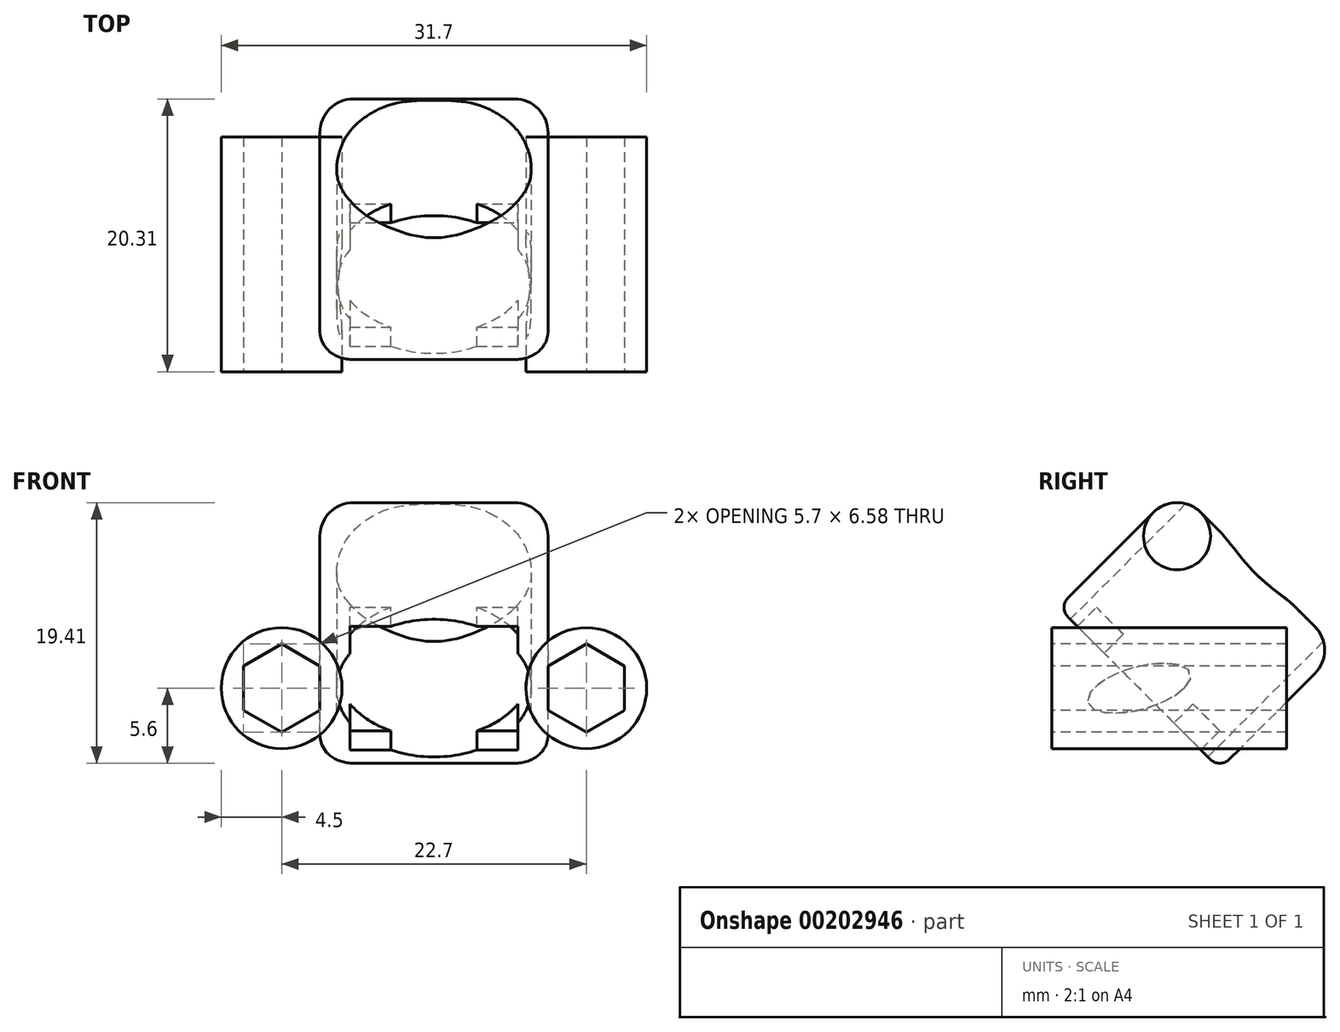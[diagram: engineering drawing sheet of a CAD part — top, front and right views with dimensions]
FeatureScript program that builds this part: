
annotation { "Feature Type Name" : "Feature", "Feature Type Description" : "" }
export const myFeature = defineFeature(function(context is Context, id is Id, definition is map)
    precondition{}
    {
        {
            var Q0;
            Q0=qCreatedBy(makeId("Top.planeOp"),FACE);
            var sketch = newSketch(context, id + "F0", { "sketchPlane" : qUnion([Q0])});
            skLineSegment(sketch, "E0.bottom", {"start": v(6.25, 6.25) * mm, "end": v(-6.25, 6.25) * mm});
            skLineSegment(sketch, "E0.top", {"start": v(6.25, -6.25) * mm, "end": v(-6.25, -6.25) * mm});
            skLineSegment(sketch, "E0.left", {"start": v(6.25, 6.25) * mm, "end": v(6.25, -6.25) * mm});
            skLineSegment(sketch, "E0.right", {"start": v(-6.25, 6.25) * mm, "end": v(-6.25, -6.25) * mm});
            skPoint(sketch, "E0.middle", {"position": v(0, 0) * mm});
            skCircle(sketch, "E1", {"center": v(0, 0) * mm, "radius": 7.25 * mm});
            skLineSegment(sketch, "E2.bottom", {"start": v(8.5, 8.5) * mm, "end": v(-8.5, 8.5) * mm});
            skLineSegment(sketch, "E2.top", {"start": v(8.5, -8.5) * mm, "end": v(-8.5, -8.5) * mm});
            skLineSegment(sketch, "E2.left", {"start": v(8.5, 8.5) * mm, "end": v(8.5, -8.5) * mm});
            skLineSegment(sketch, "E2.right", {"start": v(-8.5, 8.5) * mm, "end": v(-8.5, -8.5) * mm});
            skSolve(sketch);
        }
        {
            var Q0;
            Q0=makeQuery(id+"F0.imprint","IMPRINT",FACE,{"disambiguationData":[TD([[makeQuery(id+"F0.imprint","IMPRINT",EDGE,{"derivedFrom":sQuery(id+"F0.wireOp",EDGE,"E2.bottom")}),1.0]])]});
            var Q1;
            {var subQ0=sQuery(id+"F0.wireOp",EDGE,"E0.right");var subQ1=sQuery(id+"F0.wireOp",EDGE,"E0.bottom");var subQ2=makeQuery(id+"F0.imprint","INTERSECT",VERTEX,{"derivedFrom":[subQ1,subQ0]});Q1=makeQuery(id+"F0.imprint","IMPRINT",FACE,{"disambiguationData":[TD([[makeQuery(id+"F0.imprint","IMPRINT",EDGE,{"disambiguationData":[TD([[subQ2,1.0]])],"derivedFrom":subQ1}),1.0]])]});}
            var Q2;
            {var subQ0=sQuery(id+"F0.wireOp",EDGE,"E0.left");var subQ1=sQuery(id+"F0.wireOp",EDGE,"E0.bottom");var subQ2=makeQuery(id+"F0.imprint","INTERSECT",VERTEX,{"derivedFrom":[subQ1,subQ0]});Q2=makeQuery(id+"F0.imprint","IMPRINT",FACE,{"disambiguationData":[TD([[makeQuery(id+"F0.imprint","IMPRINT",EDGE,{"disambiguationData":[TD([[subQ2,-1.0]])],"derivedFrom":subQ1}),1.0]])]});}
            var Q3;
            {var subQ0=sQuery(id+"F0.wireOp",EDGE,"E0.left");var subQ1=sQuery(id+"F0.wireOp",EDGE,"E0.top");var subQ2=makeQuery(id+"F0.imprint","INTERSECT",VERTEX,{"derivedFrom":[subQ1,subQ0]});Q3=makeQuery(id+"F0.imprint","IMPRINT",FACE,{"disambiguationData":[TD([[makeQuery(id+"F0.imprint","IMPRINT",EDGE,{"disambiguationData":[TD([[subQ2,-1.0]])],"derivedFrom":subQ1}),-1.0]])]});}
            var Q4;
            {var subQ0=sQuery(id+"F0.wireOp",EDGE,"E0.right");var subQ1=sQuery(id+"F0.wireOp",EDGE,"E0.top");var subQ2=makeQuery(id+"F0.imprint","INTERSECT",VERTEX,{"derivedFrom":[subQ1,subQ0]});Q4=makeQuery(id+"F0.imprint","IMPRINT",FACE,{"disambiguationData":[TD([[makeQuery(id+"F0.imprint","IMPRINT",EDGE,{"disambiguationData":[TD([[subQ2,1.0]])],"derivedFrom":subQ1}),-1.0]])]});}
            extrude(context, id + "F1", {"entities" : qUnion([Q0, Q1, Q2, Q3, Q4]), "depth" : 12.5 * mm});
        }
        {
            var Q0;
            Q0=qCreatedBy(makeId("Top.planeOp"),FACE);
            var sketch = newSketch(context, id + "F2", { "sketchPlane" : qUnion([Q0])});
            skLineSegment(sketch, "E3", {"start": v(-15.14, 0) * mm, "end": v(14.33, 0) * mm});
            skSolve(sketch);
        }
        {
            var Q0;
            Q0=qCreatedBy(makeId("Front.planeOp"),FACE);
            var sketch = newSketch(context, id + "F3", { "sketchPlane" : qUnion([Q0])});
            skCircle(sketch, "E4", {"center": v(-11.35, 0) * mm, "radius": 4.5 * mm});
            skCircle(sketch, "E5.cCircle", {"center": v(-11.35, 0) * mm, "radius": 2.85 * mm, "construction": true});
            skLineSegment(sketch, "E5.0", {"start": v(-8.5, 1.65) * mm, "end": v(-8.5, -1.65) * mm});
            skLineSegment(sketch, "E5.1", {"start": v(-8.5, -1.65) * mm, "end": v(-11.35, -3.3) * mm});
            skLineSegment(sketch, "E5.2", {"start": v(-11.35, -3.3) * mm, "end": v(-14.2, -1.65) * mm});
            skLineSegment(sketch, "E5.3", {"start": v(-14.2, -1.65) * mm, "end": v(-14.2, 1.65) * mm});
            skLineSegment(sketch, "E5.4", {"start": v(-14.2, 1.65) * mm, "end": v(-11.35, 3.3) * mm});
            skLineSegment(sketch, "E5.5", {"start": v(-11.35, 3.3) * mm, "end": v(-8.5, 1.65) * mm});
            skPoint(sketch, "E5.0.midPoint", {"position": v(-8.5, 0) * mm});
            skCircle(sketch, "E6.1.0.0", {"center": v(11.35, 0) * mm, "radius": 4.5 * mm});
            skLineSegment(sketch, "E6.direction1", {"start": v(-11.35, 0) * mm, "end": v(11.35, 0) * mm, "construction": true});
            skLineSegment(sketch, "E7.1.0.0", {"start": v(11.35, -3.3) * mm, "end": v(8.5, -1.65) * mm});
            skLineSegment(sketch, "E7.1.0.1", {"start": v(14.2, -1.65) * mm, "end": v(11.35, -3.3) * mm});
            skLineSegment(sketch, "E7.1.0.2", {"start": v(14.2, 1.65) * mm, "end": v(14.2, -1.65) * mm});
            skLineSegment(sketch, "E7.1.0.3", {"start": v(11.35, 3.3) * mm, "end": v(14.2, 1.65) * mm});
            skLineSegment(sketch, "E7.1.0.4", {"start": v(8.5, 1.65) * mm, "end": v(11.35, 3.3) * mm});
            skLineSegment(sketch, "E7.1.0.5", {"start": v(8.5, -1.65) * mm, "end": v(8.5, 1.65) * mm});
            skLineSegment(sketch, "E7.direction1", {"start": v(-14.2, -1.65) * mm, "end": v(8.5, -1.65) * mm, "construction": true});
            skPoint(sketch, "E8.0.1.0", {"position": v(-8.5, -41.3) * mm});
            skLineSegment(sketch, "E8.0.1.2", {"start": v(11.35, -38) * mm, "end": v(14.2, -39.65) * mm});
            skLineSegment(sketch, "E8.0.1.3", {"start": v(8.5, -39.65) * mm, "end": v(11.35, -38) * mm});
            skLineSegment(sketch, "E8.0.1.4", {"start": v(8.5, -42.95) * mm, "end": v(8.5, -39.65) * mm});
            skCircle(sketch, "E8.0.1.5", {"center": v(-11.35, -41.3) * mm, "radius": 4.5 * mm});
            skCircle(sketch, "E8.0.1.6", {"center": v(-11.35, -41.3) * mm, "radius": 2.85 * mm, "construction": true});
            skCircle(sketch, "E8.0.1.7", {"center": v(11.35, -41.3) * mm, "radius": 4.5 * mm});
            skLineSegment(sketch, "E8.0.1.8", {"start": v(-11.35, -41.3) * mm, "end": v(11.35, -41.3) * mm, "construction": true});
            skLineSegment(sketch, "E8.0.1.9", {"start": v(11.35, -44.6) * mm, "end": v(8.5, -42.95) * mm});
            skLineSegment(sketch, "E8.0.1.10", {"start": v(14.2, -42.95) * mm, "end": v(11.35, -44.6) * mm});
            skLineSegment(sketch, "E8.0.1.11", {"start": v(14.2, -39.65) * mm, "end": v(14.2, -42.95) * mm});
            skLineSegment(sketch, "E8.0.1.12", {"start": v(-8.5, -39.65) * mm, "end": v(-8.5, -42.95) * mm});
            skLineSegment(sketch, "E8.0.1.13", {"start": v(-8.5, -42.95) * mm, "end": v(-11.35, -44.6) * mm});
            skLineSegment(sketch, "E8.0.1.14", {"start": v(-11.35, -44.6) * mm, "end": v(-14.2, -42.95) * mm});
            skLineSegment(sketch, "E8.0.1.15", {"start": v(-14.2, -42.95) * mm, "end": v(-14.2, -39.65) * mm});
            skLineSegment(sketch, "E8.0.1.16", {"start": v(-14.2, -39.65) * mm, "end": v(-11.35, -38) * mm});
            skLineSegment(sketch, "E8.0.1.17", {"start": v(-11.35, -38) * mm, "end": v(-8.5, -39.65) * mm});
            skLineSegment(sketch, "E8.direction1", {"start": v(-14.2, -1.65) * mm, "end": v(10.8, -1.65) * mm, "construction": true});
            skLineSegment(sketch, "E8.direction2", {"start": v(-14.2, -1.65) * mm, "end": v(-14.2, -42.95) * mm, "construction": true});
            skLineSegment(sketch, "E9", {"start": v(22.71, -41.3) * mm, "end": v(-23, -41.3) * mm, "construction": true});
            skArc(sketch, "E10", {"start": v(15.85, -41.3) * mm, "mid": v(16.07, -41.21) * mm, "end": v(16.28, -41.13) * mm});
            skLineSegment(sketch, "E11.bottom", {"start": v(-18, -2.65) * mm, "end": v(18, -2.65) * mm});
            skLineSegment(sketch, "E11.top", {"start": v(-18, -38.65) * mm, "end": v(18, -38.65) * mm});
            skLineSegment(sketch, "E11.left", {"start": v(-18, -2.65) * mm, "end": v(-18, -38.65) * mm});
            skLineSegment(sketch, "E11.right", {"start": v(18, -2.65) * mm, "end": v(18, -38.65) * mm});
            skPoint(sketch, "E11.middle", {"position": v(0, -20.65) * mm});
            skLineSegment(sketch, "E12", {"start": v(20, -5.72) * mm, "end": v(20, -35.58) * mm});
            skArc(sketch, "E13.trimOffspring", {"start": v(16.28, -0.17) * mm, "mid": v(16.07, -0.09) * mm, "end": v(15.85, 0) * mm});
            skPoint(sketch, "E14.visualSharp", {"position": v(20, -2.13) * mm});
            skArc(sketch, "E14.filletArc", {"start": v(20, -5.72) * mm, "mid": v(18.98, -2.38) * mm, "end": v(16.28, -0.17) * mm});
            skPoint(sketch, "E15.visualSharp", {"position": v(20, -39.17) * mm});
            skArc(sketch, "E15.filletArc", {"start": v(16.28, -41.13) * mm, "mid": v(18.98, -38.92) * mm, "end": v(20, -35.58) * mm});
            skArc(sketch, "E16.0", {"start": v(15.55, -42.92) * mm, "mid": v(19.83, -40.3) * mm, "end": v(21.5, -35.58) * mm});
            skLineSegment(sketch, "E16.1", {"start": v(21.5, -5.72) * mm, "end": v(21.5, -35.58) * mm});
            skArc(sketch, "E16.2", {"start": v(21.5, -5.72) * mm, "mid": v(19.83, -1) * mm, "end": v(15.55, 1.62) * mm});
            skArc(sketch, "E17.MirrorCS", {"start": v(-16.28, -0.17) * mm, "mid": v(-16.07, -0.09) * mm, "end": v(-15.85, 0) * mm});
            skArc(sketch, "E18.MirrorCS", {"start": v(-15.85, -41.3) * mm, "mid": v(-16.07, -41.21) * mm, "end": v(-16.28, -41.13) * mm});
            skArc(sketch, "E19.MirrorCS", {"start": v(-16.28, -41.13) * mm, "mid": v(-18.98, -38.92) * mm, "end": v(-20, -35.58) * mm});
            skArc(sketch, "E20.MirrorCS", {"start": v(-15.55, -42.92) * mm, "mid": v(-19.83, -40.3) * mm, "end": v(-21.5, -35.58) * mm});
            skArc(sketch, "E21.MirrorCS", {"start": v(-21.5, -5.72) * mm, "mid": v(-19.83, -1) * mm, "end": v(-15.55, 1.62) * mm});
            skArc(sketch, "E22.MirrorCS", {"start": v(-20, -5.72) * mm, "mid": v(-18.98, -2.38) * mm, "end": v(-16.28, -0.17) * mm});
            skLineSegment(sketch, "E23.MirrorCS", {"start": v(-21.5, -5.72) * mm, "end": v(-21.5, -35.58) * mm});
            skLineSegment(sketch, "E24.MirrorCS", {"start": v(-20, -5.72) * mm, "end": v(-20, -35.58) * mm});
            skLineSegment(sketch, "E25", {"start": v(7.16, -42.95) * mm, "end": v(-7.16, -42.95) * mm});
            skLineSegment(sketch, "E26.0", {"start": v(6.85, -41.45) * mm, "end": v(-6.85, -41.45) * mm});
            skSolve(sketch);
        }
        {
            var Q0;
            {var subQ0=sQuery(id+"F0.wireOp",EDGE,"E0.left");var subQ1=sQuery(id+"F0.wireOp",EDGE,"E0.bottom");var subQ2=makeQuery(id+"F0.imprint","INTERSECT",VERTEX,{"derivedFrom":[subQ1,subQ0]});Q0=makeQuery(id+"F0.imprint","IMPRINT",FACE,{"disambiguationData":[TD([[makeQuery(id+"F0.imprint","IMPRINT",EDGE,{"disambiguationData":[TD([[subQ2,-1.0]])],"derivedFrom":subQ1}),1.0]])]});}
            var Q1;
            {var subQ0=sQuery(id+"F0.wireOp",EDGE,"E0.right");var subQ1=sQuery(id+"F0.wireOp",EDGE,"E0.bottom");var subQ2=makeQuery(id+"F0.imprint","INTERSECT",VERTEX,{"derivedFrom":[subQ1,subQ0]});Q1=makeQuery(id+"F0.imprint","IMPRINT",FACE,{"disambiguationData":[TD([[makeQuery(id+"F0.imprint","IMPRINT",EDGE,{"disambiguationData":[TD([[subQ2,1.0]])],"derivedFrom":subQ1}),1.0]])]});}
            var Q2;
            {var subQ0=sQuery(id+"F0.wireOp",EDGE,"E0.right");var subQ1=sQuery(id+"F0.wireOp",EDGE,"E0.top");var subQ2=makeQuery(id+"F0.imprint","INTERSECT",VERTEX,{"derivedFrom":[subQ1,subQ0]});Q2=makeQuery(id+"F0.imprint","IMPRINT",FACE,{"disambiguationData":[TD([[makeQuery(id+"F0.imprint","IMPRINT",EDGE,{"disambiguationData":[TD([[subQ2,1.0]])],"derivedFrom":subQ1}),-1.0]])]});}
            var Q3;
            {var subQ0=sQuery(id+"F0.wireOp",EDGE,"E0.left");var subQ1=sQuery(id+"F0.wireOp",EDGE,"E0.top");var subQ2=makeQuery(id+"F0.imprint","INTERSECT",VERTEX,{"derivedFrom":[subQ1,subQ0]});Q3=makeQuery(id+"F0.imprint","IMPRINT",FACE,{"disambiguationData":[TD([[makeQuery(id+"F0.imprint","IMPRINT",EDGE,{"disambiguationData":[TD([[subQ2,-1.0]])],"derivedFrom":subQ1}),-1.0]])]});}
            extrude(context, id + "F4", {"entities" : qUnion([Q0, Q1, Q2, Q3]), "operationType" : NewBodyOperationType.REMOVE, "depth" : 2 * mm});
        }
        {
            var Q0;
            Q0=makeQuery(id+"F1.opExtrude","CAP_EDGE",EDGE,{"disambiguationData":[OSD([sQuery(id+"F0.wireOp",EDGE,"E2.right")])],"isStart":false});
            var Q1;
            Q1=makeQuery(id+"F1.opExtrude","CAP_EDGE",EDGE,{"disambiguationData":[OSD([sQuery(id+"F0.wireOp",EDGE,"E2.bottom")])],"isStart":false});
            var Q2;
            Q2=makeQuery(id+"F1.opExtrude","CAP_EDGE",EDGE,{"disambiguationData":[OSD([sQuery(id+"F0.wireOp",EDGE,"E2.left")])],"isStart":false});
            var Q3;
            Q3=makeQuery(id+"F1.opExtrude","CAP_EDGE",EDGE,{"disambiguationData":[OSD([sQuery(id+"F0.wireOp",EDGE,"E2.top")])],"isStart":false});
            var Q4;
            Q4=makeQuery(id+"F1.opExtrude","SWEPT_EDGE",EDGE,{"disambiguationData":[OSD([sQuery(id+"F0.wireOp",EDGE,"E2.bottom"),sQuery(id+"F0.wireOp",EDGE,"E2.right")])]});
            var Q5;
            Q5=makeQuery(id+"F1.opExtrude","SWEPT_EDGE",EDGE,{"disambiguationData":[OSD([sQuery(id+"F0.wireOp",EDGE,"E2.bottom"),sQuery(id+"F0.wireOp",EDGE,"E2.left")])]});
            var Q6;
            Q6=makeQuery(id+"F1.opExtrude","SWEPT_EDGE",EDGE,{"disambiguationData":[OSD([sQuery(id+"F0.wireOp",EDGE,"E2.top"),sQuery(id+"F0.wireOp",EDGE,"E2.right")])]});
            var Q7;
            Q7=makeQuery(id+"F1.opExtrude","SWEPT_EDGE",EDGE,{"disambiguationData":[OSD([sQuery(id+"F0.wireOp",EDGE,"E2.top"),sQuery(id+"F0.wireOp",EDGE,"E2.left")])]});
            fillet(context, id + "F5", {"entities" : qUnion([Q0, Q1, Q2, Q3, Q4, Q5, Q6, Q7]), "radius" : 2.5 * mm, "tangentPropagation" : true, "allowEdgeOverflow" : false});
        }
        {
            var Q0;
            Q0=makeQuery(id+"F1.opExtrude","SWEPT_BODY",BODY,{"disambiguationData":[OSD([sQuery(id+"F0.wireOp",EDGE,"E2.bottom"),sQuery(id+"F0.wireOp",EDGE,"E2.top"),sQuery(id+"F0.wireOp",EDGE,"E2.left"),sQuery(id+"F0.wireOp",EDGE,"E2.right")])]});
            var Q1;
            Q1=sQuery(id+"F2.wireOp",EDGE,"E3");
            transform(context, id + "F6", {"entities" : qUnion([Q0]), "transformType" : TransformType.ROTATION, "transformAxis" : qUnion([Q1]), "angle" : 45 * degree, "oppositeDirection" : true, "makeCopy" : false});
        }
        {
            var Q0;
            Q0=makeQuery(id+"F3.imprint","IMPRINT",FACE,{"disambiguationData":[TD([[makeQuery(id+"F3.imprint","IMPRINT",EDGE,{"derivedFrom":sQuery(id+"F3.wireOp",EDGE,"E6.1.0.0")}),1.0]])]});
            var Q1;
            Q1=makeQuery(id+"F3.imprint","IMPRINT",FACE,{"disambiguationData":[TD([[makeQuery(id+"F3.imprint","IMPRINT",EDGE,{"derivedFrom":sQuery(id+"F3.wireOp",EDGE,"E4")}),1.0]])]});
            var Q2;
            {var subQ0=sQuery(id+"F3.wireOp",EDGE,"E11.bottom");var subQ1=sQuery(id+"F3.wireOp",EDGE,"E6.1.0.0");var subQ2=makeQuery(id+"F3.imprint","INTERSECT",VERTEX,{"disambiguationData":[OD(0.0)],"derivedFrom":[subQ1,subQ0]});Q2=makeQuery(id+"F3.imprint","IMPRINT",FACE,{"disambiguationData":[TD([[makeQuery(id+"F3.imprint","IMPRINT",EDGE,{"disambiguationData":[TD([[subQ2,-1.0]])],"derivedFrom":subQ1}),1.0]])]});}
            var Q3;
            {var subQ0=sQuery(id+"F3.wireOp",EDGE,"E11.bottom");var subQ1=sQuery(id+"F3.wireOp",EDGE,"E4");var subQ8=makeQuery(id+"F3.imprint","INTERSECT",VERTEX,{"disambiguationData":[OD(0.0)],"derivedFrom":[subQ1,subQ0]});Q3=makeQuery(id+"F3.imprint","IMPRINT",FACE,{"disambiguationData":[TD([[makeQuery(id+"F3.imprint","IMPRINT",EDGE,{"disambiguationData":[TD([[subQ8,1.0]])],"derivedFrom":subQ1}),1.0]])]});}
            var Q4;
            Q4=makeQuery(id+"F5.opFillet","BLEND_FACE",FACE,{"disambiguationData":[OSD([sQuery(id+"F0.wireOp",EDGE,"E2.bottom")])]});
            extrude(context, id + "F7", {"entities" : qUnion([Q0, Q1, Q2, Q3]), "oppositeDirection" : true, "endBoundEntityFace" : qUnion([Q4]), "depth" : 11 * mm, "hasSecondDirection" : true, "secondDirectionOppositeDirection" : false, "secondDirectionDepth" : 6.5 * mm});
        }
        {
            var Q0;
            Q0=makeQuery(id+"F4.boolean.opBoolean","COPY",FACE,{"derivedFrom":makeQuery(id+"F4.opExtrude","CAP_FACE",FACE,{"disambiguationData":[OSD([sQuery(id+"F0.wireOp",EDGE,"E0.bottom"),sQuery(id+"F0.wireOp",EDGE,"E0.right"),sQuery(id+"F0.wireOp",EDGE,"E1")])],"isStart":false})});
            var sketch = newSketch(context, id + "F8", { "sketchPlane" : qUnion([Q0])});
            skLineSegment(sketch, "E27.bottom", {"start": v(-6.25, -6.5) * mm, "end": v(6.25, -6.5) * mm});
            skLineSegment(sketch, "E27.top", {"start": v(-6.25, 6.5) * mm, "end": v(6.25, 6.5) * mm});
            skLineSegment(sketch, "E27.left", {"start": v(-6.25, -6.5) * mm, "end": v(-6.25, 6.5) * mm});
            skLineSegment(sketch, "E27.right", {"start": v(6.25, -6.5) * mm, "end": v(6.25, 6.5) * mm});
            skPoint(sketch, "E27.middle", {"position": v(0, 0) * mm});
            skCircle(sketch, "E28", {"center": v(0, 0) * mm, "radius": 7.25 * mm});
            skSolve(sketch);
        }
        {
            var Q0;
            {var subQ1=sQuery(id+"F0.wireOp",EDGE,"E1");var subQ2=sQuery(id+"F0.wireOp",EDGE,"E0.bottom");var subQ4=makeQuery(id+"F4.boolean.opBoolean","COPY",EDGE,{"derivedFrom":makeQuery(id+"F4.opExtrude","CAP_EDGE",EDGE,{"disambiguationData":[OSD([subQ1]),TDD([makeQuery(id+"F0.imprint","IMPRINT",EDGE,{"disambiguationData":[TD([[makeQuery(id+"F0.imprint","INTERSECT",VERTEX,{"derivedFrom":[subQ2,subQ1]}),-1.0]])],"derivedFrom":subQ1})])],"isStart":false})});Q0=makeQuery(id+"F8.imprint","IMPRINT",FACE,{"disambiguationData":[TD([[makeQuery(id+"F8.imprint","IMPRINT",EDGE,{"derivedFrom":subQ4}),1.0]])]});}
            var Q1;
            {var subQ5=sQuery(id+"F8.wireOp",EDGE,"E27.top");Q1=makeQuery(id+"F8.imprint","IMPRINT",FACE,{"disambiguationData":[TD([[makeQuery(id+"F8.imprint","IMPRINT",EDGE,{"derivedFrom":subQ5}),-1.0]])]});}
            extrude(context, id + "F9", {"entities" : qUnion([Q0, Q1]), "operationType" : NewBodyOperationType.REMOVE, "depth" : 25 * mm});
        }
        {
            var Q0;
            Q0=qSketchRegion(id+"F8",true);
            extrude(context, id + "F10", {"entities" : qUnion([Q0]), "operationType" : NewBodyOperationType.REMOVE, "depth" : 25 * mm});
        }
        {
            var Q0;
            {var subQ0=sQuery(id+"F8.wireOp",EDGE,"E28");var subQ1=makeQuery(id+"F8.imprint","INTERSECT",VERTEX,{"derivedFrom":[sQuery(id+"F8.wireOp",EDGE,"E27.top"),subQ0]});var subQ2=makeQuery(id+"F8.imprint","INTERSECT",VERTEX,{"derivedFrom":[sQuery(id+"F8.wireOp",EDGE,"E27.right"),subQ0]});Q0=makeQuery(id+"F8.imprint","IMPRINT",FACE,{"disambiguationData":[TD([[makeQuery(id+"F8.imprint","IMPRINT",EDGE,{"disambiguationData":[TD([[subQ1,1.0],[subQ2,-1.0]])],"derivedFrom":subQ0}),1.0]])]});}
            extrude(context, id + "F11", {"entities" : qUnion([Q0]), "operationType" : NewBodyOperationType.REMOVE, "oppositeDirection" : true, "depth" : 25 * mm});
        }
        {
            var Q0;
            Q0=makeQuery(id+"F1.opExtrude","CAP_EDGE",EDGE,{"disambiguationData":[OSD([sQuery(id+"F0.wireOp",EDGE,"E2.bottom")])],"isStart":true});
            var Q1;
            Q1=makeQuery(id+"F1.opExtrude","CAP_EDGE",EDGE,{"disambiguationData":[OSD([sQuery(id+"F0.wireOp",EDGE,"E2.top")])],"isStart":true});
            fillet(context, id + "F12", {"entities" : qUnion([Q0, Q1]), "radius" : 1 * mm, "tangentPropagation" : true, "allowEdgeOverflow" : false});
        }
        {
            var Q0;
            {var subQ0=sQuery(id+"F8.wireOp",EDGE,"E28");var subQ6=sQuery(id+"F8.wireOp",EDGE,"E27.bottom");var subQ7=makeQuery(id+"F8.imprint","INTERSECT",VERTEX,{"disambiguationData":[OD(0.0)],"derivedFrom":[subQ6,subQ0]});Q0=makeQuery(id+"F8.imprint","IMPRINT",FACE,{"disambiguationData":[TD([[makeQuery(id+"F8.imprint","IMPRINT",EDGE,{"disambiguationData":[TD([[subQ7,-1.0]])],"derivedFrom":subQ6}),1.0]])]});}
            var Q1;
            {var subQ0=sQuery(id+"F8.wireOp",EDGE,"E28");var subQ1=sQuery(id+"F8.wireOp",EDGE,"E27.left");var subQ2=makeQuery(id+"F8.imprint","INTERSECT",VERTEX,{"disambiguationData":[OD(0.0)],"derivedFrom":[subQ1,subQ0]});Q1=makeQuery(id+"F8.imprint","IMPRINT",FACE,{"disambiguationData":[TD([[makeQuery(id+"F8.imprint","IMPRINT",EDGE,{"disambiguationData":[TD([[subQ2,-1.0]])],"derivedFrom":subQ1}),1.0]])]});}
            var Q2;
            {var subQ0=sQuery(id+"F8.wireOp",EDGE,"E28");var subQ1=sQuery(id+"F8.wireOp",EDGE,"E27.bottom");var subQ2=makeQuery(id+"F8.imprint","INTERSECT",VERTEX,{"disambiguationData":[OD(0.0)],"derivedFrom":[subQ1,subQ0]});Q2=makeQuery(id+"F8.imprint","IMPRINT",FACE,{"disambiguationData":[TD([[makeQuery(id+"F8.imprint","IMPRINT",EDGE,{"disambiguationData":[TD([[subQ2,-1.0]])],"derivedFrom":subQ1}),-1.0]])]});}
            var Q3;
            {var subQ0=sQuery(id+"F8.wireOp",EDGE,"E28");var subQ1=sQuery(id+"F8.wireOp",EDGE,"E27.top");var subQ2=makeQuery(id+"F8.imprint","INTERSECT",VERTEX,{"disambiguationData":[OD(0.0)],"derivedFrom":[subQ1,subQ0]});Q3=makeQuery(id+"F8.imprint","IMPRINT",FACE,{"disambiguationData":[TD([[makeQuery(id+"F8.imprint","IMPRINT",EDGE,{"disambiguationData":[TD([[subQ2,-1.0]])],"derivedFrom":subQ1}),1.0]])]});}
            var Q4;
            {var subQ0=sQuery(id+"F8.wireOp",EDGE,"E28");var subQ1=sQuery(id+"F8.wireOp",EDGE,"E27.right");var subQ2=makeQuery(id+"F8.imprint","INTERSECT",VERTEX,{"disambiguationData":[OD(0.0)],"derivedFrom":[subQ1,subQ0]});Q4=makeQuery(id+"F8.imprint","IMPRINT",FACE,{"disambiguationData":[TD([[makeQuery(id+"F8.imprint","IMPRINT",EDGE,{"disambiguationData":[TD([[subQ2,-1.0]])],"derivedFrom":subQ1}),-1.0]])]});}
            extrude(context, id + "F13", {"entities" : qUnion([Q0, Q1, Q2, Q3, Q4]), "operationType" : NewBodyOperationType.REMOVE, "oppositeDirection" : true, "depth" : 25 * mm, "symmetric" : true});
        }
    });
